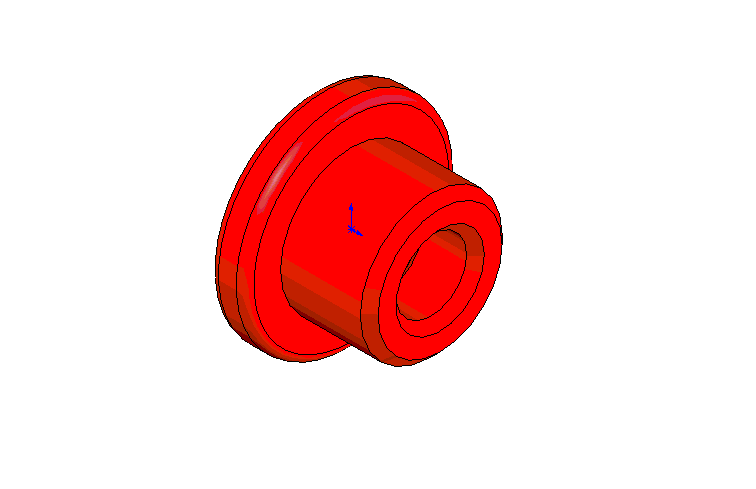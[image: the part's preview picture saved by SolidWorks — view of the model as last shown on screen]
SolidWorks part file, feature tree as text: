
SOLIDWORKS PART (.sldprt)
format: sldprt  version: not decoded by parser v0  size: 216,576 bytes
history: native  units: mm
features: plane x3, sketch x3, extrude x2, material x1, cut_extrude x1, chamfer x1, fillet x1 (+10 scaffold rows collapsed)
feature tree (22):
  scaffold x10  (default folders/planes/origin — collapsed)
  material  "Matériau <non spécifié>"
  plane  "Plan de face"
  plane  "Plan de dessus"
  plane  "Plan de droite"
  sketch  "Esquisse1"  dims[D1=4.0mm D2=8.0mm]
  extrude  "Extrusion1"  Depth=5mm
  sketch  "Esquisse2"  dims[D1=12.0mm]
  extrude  "Extrusion3"  [1 undecoded]
  sketch  "Esquisse3"  dims[D1=5.0mm]
  cut_extrude  "Enlèv. mat.-Extru.1"  Depth=3.5mm
  chamfer  "Chanfrein1"  Distance=0.5mm Angle=45deg
  fillet  "Congé1"  Radius=0.5mm
decode coverage: 7 of 8 modeling features carry decoded parameters
note: 1 parameter value undecoded
note: suppression state not decoded; provenance and decode notes live in map.json
